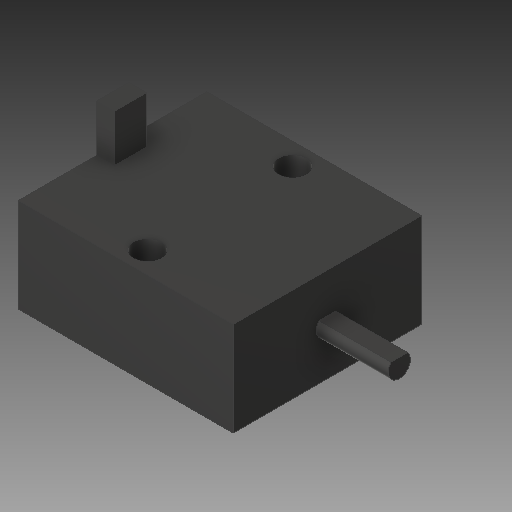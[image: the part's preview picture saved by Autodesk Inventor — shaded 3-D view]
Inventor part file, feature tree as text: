
AUTODESK INVENTOR PART (.ipt)
format: ipt  version: 2018 (Build 220112000, 112)  size: 124,416 bytes
history: native  units: in
note: dims shown in document units (in); Inventor stores cm internally (conversion verified against a paired STEP export)
features: sketch x4, extrude x3, hole x1
ambient origin geometry x8: Origin, YZ Plane, XZ Plane, XY Plane, X Axis, Y Axis, Z Axis, Center Point
bodies: Solid1 (feature_tree)
feature tree (8):
  extrude  "Extrusion1"  Depth=1.0in
  hole  "Hole1"  [1 undecoded]
  extrude  "Extrusion3"  Depth=0.25in
  extrude  "Extrusion4"  Depth=0.25in
  sketch  "Sketch1"  dims[d0=1.14in d1=1.0in]
  sketch  "Sketch2"  dims[d2=0.5in d3=0.0in d4=0.385in]
  sketch  "Sketch3"  dims[d5=0.77in]
  sketch  "Sketch4"  dims[d6=0.15in d7=0.75in d8=0.279in d9=0.093in d10=0.5635in d11=1.0in d12=0.8108in d13=0.1181in d14=0.25in d15=0.5in d18=0.0394in d19=0.3819in d20=0.0in d21=0.25in d22=0.0in]
note: 1 required parameter value undecoded (feature->parameter linkage not recoverable at this tier; creation-order binding heuristic only, values carry confidence <= 0.55)
